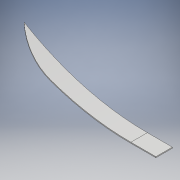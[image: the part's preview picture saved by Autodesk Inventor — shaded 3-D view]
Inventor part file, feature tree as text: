
AUTODESK INVENTOR PART (.ipt)
format: ipt  version: 2018 (Build 220112000, 112)  size: 137,216 bytes
history: native  units: mm
features: other x5, projected_geometry x2, extrude x1, sketch x1
ambient origin geometry x8: Origin, YZ Plane, XZ Plane, XY Plane, X Axis, Y Axis, Z Axis, Center Point
bodies: Body1 (feature_tree)
feature tree (9):
  other  "endplate_ver2.ipt"
  extrude  "押し出し1"  Depth=10.0mm
  other  "面を削除1"
  other  "ソリッド2::endplate_ver2.ipt"
  other  "TaggingFeature1"
  sketch  "スケッチ1"
  projected_geometry  "投影ループ1"
  projected_geometry  "投影ループ2"
  other  "ソリッド1"
